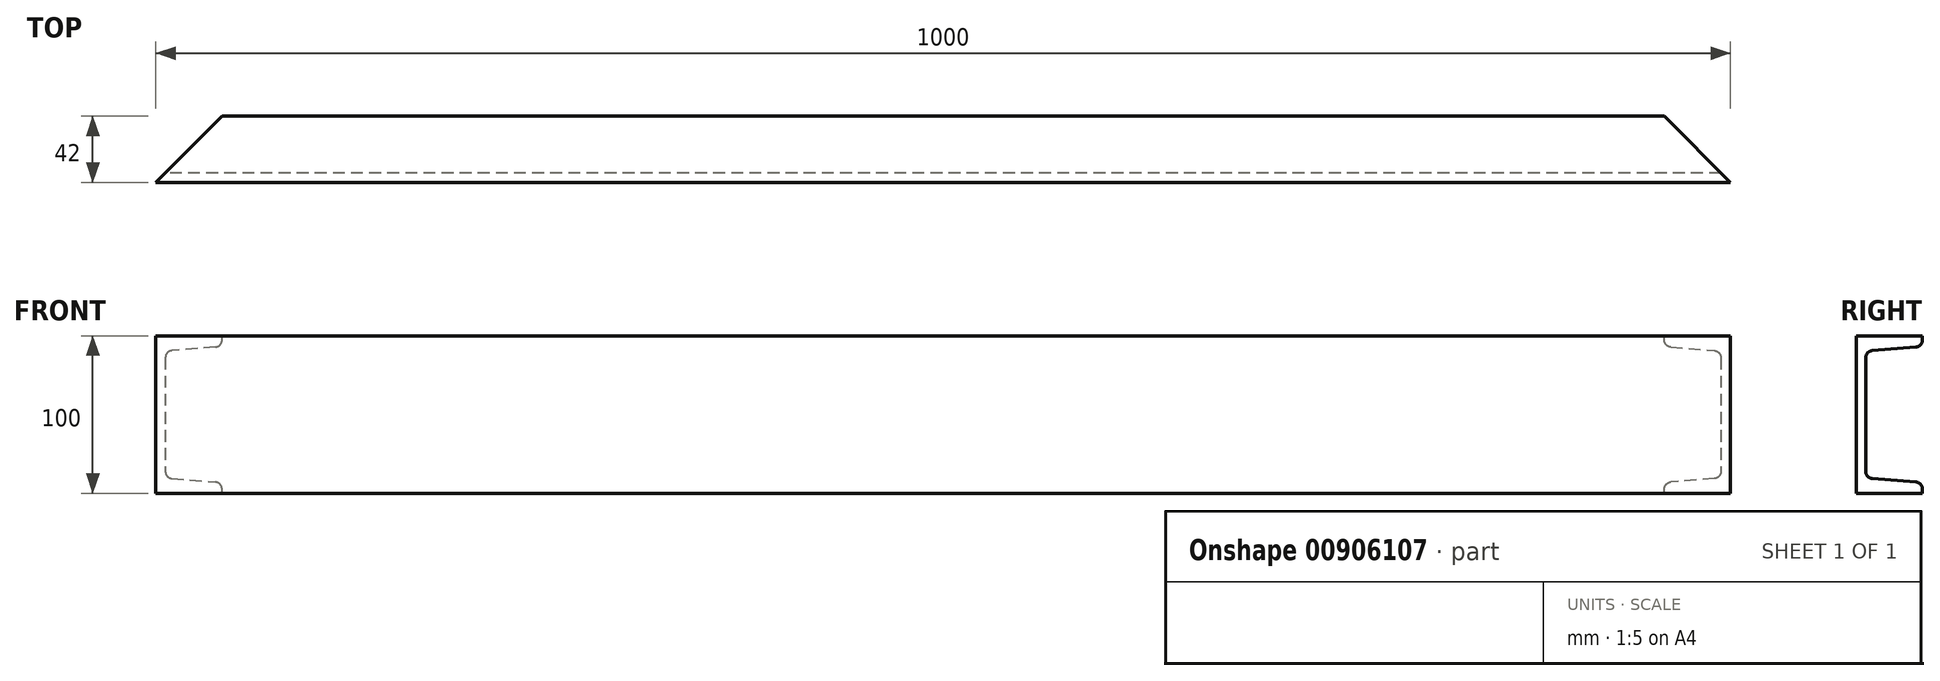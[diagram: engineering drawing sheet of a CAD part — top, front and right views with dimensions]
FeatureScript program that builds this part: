
annotation { "Feature Type Name" : "Feature", "Feature Type Description" : "" }
export const myFeature = defineFeature(function(context is Context, id is Id, definition is map)
    precondition{}
    {
        {
            var Q0;
            Q0=qCreatedBy(makeId("Right.planeOp"),FACE);
            var sketch = newSketch(context, id + "F0", { "sketchPlane" : qUnion([Q0])});
            skLineSegment(sketch, "E0", {"start": v(0, 0) * mm, "end": v(0, 100) * mm});
            skLineSegment(sketch, "E1", {"start": v(0, 100) * mm, "end": v(42, 100) * mm});
            skLineSegment(sketch, "E2", {"start": v(42, 100) * mm, "end": v(42, 97.34) * mm});
            skLineSegment(sketch, "E3", {"start": v(37.86, 92.85) * mm, "end": v(10.14, 90.63) * mm});
            skLineSegment(sketch, "E4", {"start": v(6, 86.15) * mm, "end": v(6, 13.85) * mm});
            skLineSegment(sketch, "E5", {"start": v(10.14, 9.37) * mm, "end": v(37.86, 7.15) * mm});
            skLineSegment(sketch, "E6", {"start": v(42, 2.66) * mm, "end": v(42, 0) * mm});
            skLineSegment(sketch, "E7", {"start": v(42, 0) * mm, "end": v(0, 0) * mm});
            skLineSegment(sketch, "E8", {"start": v(21, 100) * mm, "end": v(21, -10.5) * mm, "construction": true});
            skPoint(sketch, "E9", {"position": v(21, 0) * mm});
            skPoint(sketch, "E10", {"position": v(21, 91.5) * mm});
            skPoint(sketch, "E11", {"position": v(21, 8.5) * mm});
            skLineSegment(sketch, "E12", {"start": v(42, 93.18) * mm, "end": v(8.97, 93.18) * mm, "construction": true});
            skLineSegment(sketch, "E13", {"start": v(42, 6.82) * mm, "end": v(11.76, 6.82) * mm, "construction": true});
            skPoint(sketch, "E14.visualSharp", {"position": v(42, 93.18) * mm});
            skArc(sketch, "E14.filletArc", {"start": v(37.86, 92.85) * mm, "mid": v(40.8, 94.28) * mm, "end": v(42, 97.34) * mm});
            skPoint(sketch, "E15.visualSharp", {"position": v(6, 90.3) * mm});
            skArc(sketch, "E15.filletArc", {"start": v(10.14, 90.63) * mm, "mid": v(7.2, 89.2) * mm, "end": v(6, 86.15) * mm});
            skPoint(sketch, "E16.visualSharp", {"position": v(6, 9.7) * mm});
            skArc(sketch, "E16.filletArc", {"start": v(6, 13.85) * mm, "mid": v(7.2, 10.8) * mm, "end": v(10.14, 9.37) * mm});
            skPoint(sketch, "E17.visualSharp", {"position": v(42, 6.82) * mm});
            skArc(sketch, "E17.filletArc", {"start": v(42, 2.66) * mm, "mid": v(40.8, 5.72) * mm, "end": v(37.86, 7.15) * mm});
            skSolve(sketch);
        }
        {
            var Q0;
            Q0 = qSketchRegion(id + "F0", true);
            extrude(context, id + "F1", {"entities" : qUnion([Q0]), "depth" : 1000 * mm, "offsetDistance" : 25 * mm});
        }
        {
            var Q0;
            Q0=makeQuery(id+"F1.opExtrude","SWEPT_FACE",FACE,{"disambiguationData":[OSD([sQuery(id+"F0.wireOp",EDGE,"E1")])]});
            var sketch = newSketch(context, id + "F2", { "sketchPlane" : qUnion([Q0])});
            skLineSegment(sketch, "E18", {"start": v(1000, 0) * mm, "end": v(958, 42) * mm});
            skLineSegment(sketch, "E19", {"start": v(958, 42) * mm, "end": v(1000, 42) * mm});
            skLineSegment(sketch, "E20", {"start": v(1000, 42) * mm, "end": v(1000, 0) * mm});
            skSolve(sketch);
        }
        {
            var Q0;
            Q0 = qSketchRegion(id + "F2", true);
            extrude(context, id + "F3", {"entities" : qUnion([Q0]), "operationType" : NewBodyOperationType.REMOVE, "endBound" : BoundingType.THROUGH_ALL, "oppositeDirection" : true, "depth" : 25 * mm, "offsetDistance" : 25 * mm});
        }
        {
            var Q0;
            Q0=makeQuery(id+"F1.opExtrude","SWEPT_FACE",FACE,{"disambiguationData":[OSD([sQuery(id+"F0.wireOp",EDGE,"E1")])]});
            var sketch = newSketch(context, id + "F4", { "sketchPlane" : qUnion([Q0])});
            skLineSegment(sketch, "E21", {"start": v(0, 0) * mm, "end": v(42, 42) * mm});
            skLineSegment(sketch, "E22", {"start": v(42, 42) * mm, "end": v(0, 42) * mm});
            skLineSegment(sketch, "E23", {"start": v(0, 42) * mm, "end": v(0, 0) * mm});
            skSolve(sketch);
        }
        {
            var Q0;
            Q0 = qSketchRegion(id + "F4", true);
            extrude(context, id + "F5", {"entities" : qUnion([Q0]), "operationType" : NewBodyOperationType.REMOVE, "endBound" : BoundingType.THROUGH_ALL, "oppositeDirection" : true, "depth" : 25 * mm, "offsetDistance" : 25 * mm});
        }
    });
